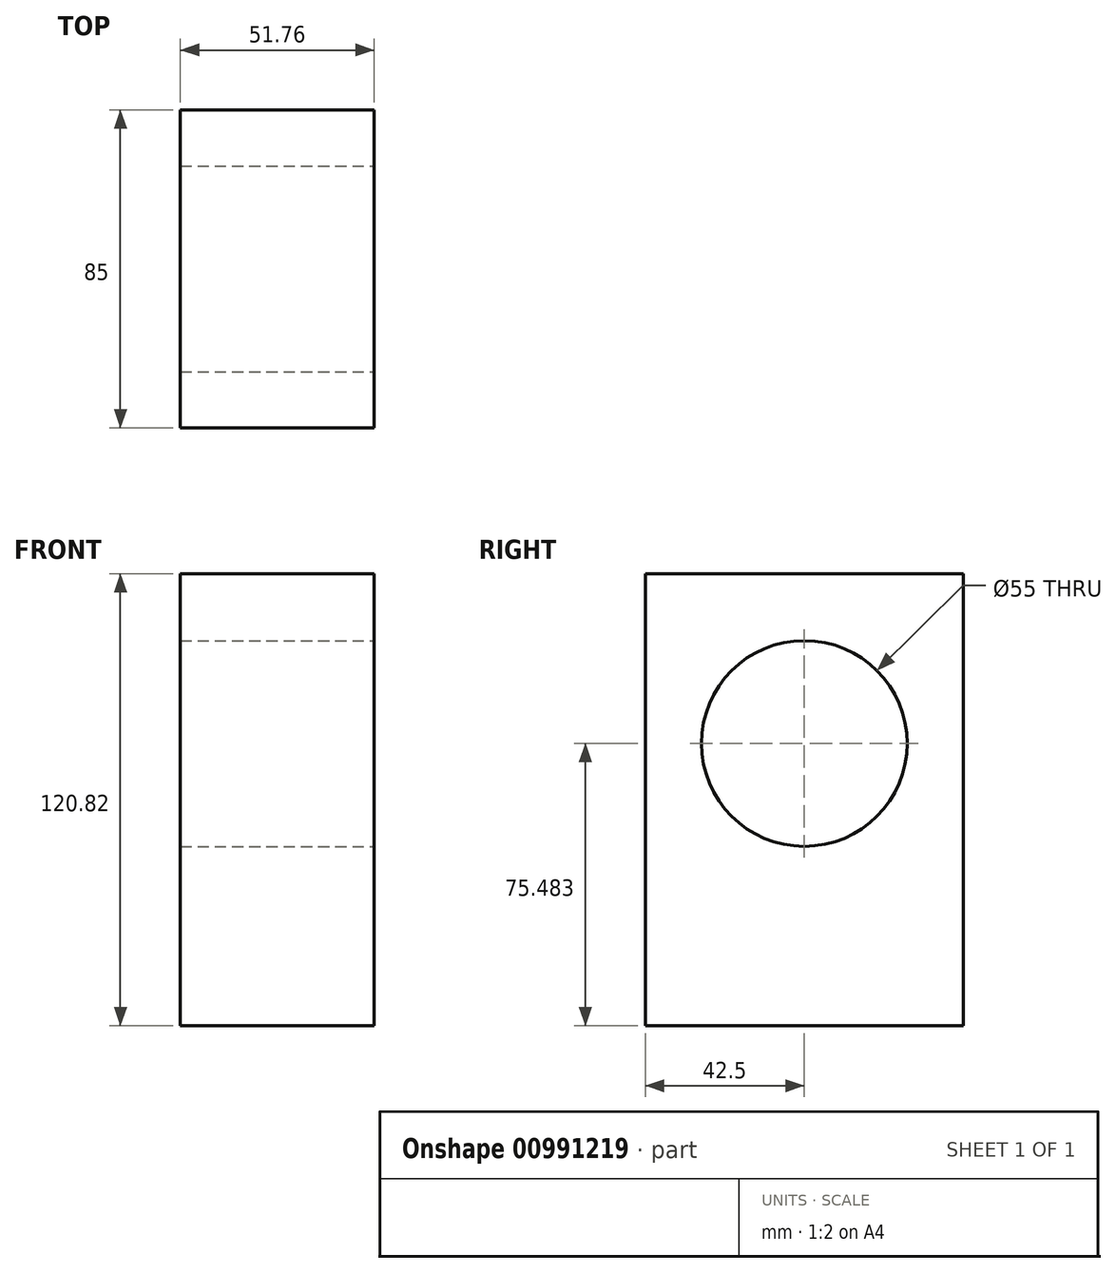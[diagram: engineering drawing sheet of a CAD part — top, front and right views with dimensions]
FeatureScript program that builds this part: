
annotation { "Feature Type Name" : "Feature", "Feature Type Description" : "" }
export const myFeature = defineFeature(function(context is Context, id is Id, definition is map)
    precondition{}
    {
        {
            var Q0;
            Q0=qCreatedBy(makeId("Front.planeOp"),FACE);
            var sketch = newSketch(context, id + "F0", { "sketchPlane" : qUnion([Q0])});
            skLineSegment(sketch, "E0.bottom", {"start": v(0, -39.2) * mm, "end": v(51.76, -39.2) * mm});
            skLineSegment(sketch, "E0.top", {"start": v(0, 81.6) * mm, "end": v(51.76, 81.6) * mm});
            skLineSegment(sketch, "E0.left", {"start": v(0, -39.2) * mm, "end": v(0, 81.6) * mm});
            skLineSegment(sketch, "E0.right", {"start": v(51.76, -39.2) * mm, "end": v(51.76, 81.6) * mm});
            skSolve(sketch);
        }
        {
            var Q0;
            Q0=makeQuery(id+"F0.imprint","IMPRINT",FACE,{"disambiguationData":[TD([[makeQuery(id+"F0.imprint","IMPRINT",EDGE,{"derivedFrom":sQuery(id+"F0.wireOp",EDGE,"E0.bottom")}),1.0]])]});
            var sketch = newSketch(context, id + "F1", { "sketchPlane" : qUnion([Q0])});
            skSolve(sketch);
        }
        {
            var Q0;
            Q0=makeQuery(id+"F1.imprint","IMPRINT",FACE,{"disambiguationData":[TD([[makeQuery(id+"F1.imprint","IMPRINT",EDGE,{"derivedFrom":makeQuery(id+"F0.imprint","IMPRINT",EDGE,{"derivedFrom":sQuery(id+"F0.wireOp",EDGE,"E0.bottom")})}),1.0]])]});
            extrude(context, id + "F2", {"entities" : qUnion([Q0]), "depth" : 85 * mm, "offsetDistance" : 25 * mm});
        }
        {
            var Q0;
            Q0=makeQuery(id+"F2.opExtrude","SWEPT_FACE",FACE,{"disambiguationData":[OSD([sQuery(id+"F0.wireOp",EDGE,"E0.right")])]});
            var sketch = newSketch(context, id + "F3", { "sketchPlane" : qUnion([Q0])});
            skCircle(sketch, "E1", {"center": v(-42.5, 36.27) * mm, "radius": 32.2 * mm});
            skPoint(sketch, "E1.centerSnap0", {"position": v(-42.5, 81.6) * mm});
            skSolve(sketch);
        }
        {
            var Q0;
            Q0=sQuery(id+"F3.wireOp",VERTEX,"E1.center");
            var Q1;
            Q1=makeQuery(id+"F2.opExtrude","SWEPT_BODY",BODY,{"disambiguationData":[OSD([sQuery(id+"F0.wireOp",EDGE,"E0.bottom"),sQuery(id+"F0.wireOp",EDGE,"E0.top"),sQuery(id+"F0.wireOp",EDGE,"E0.left"),sQuery(id+"F0.wireOp",EDGE,"E0.right")])]});
            hole(context, id + "F4", {"style" : HoleStyle.SIMPLE, "endStyle" : HoleEndStyle.THROUGH, "holeDiameter" : 55 * mm, "majorDiameter" : 5 * mm, "isTappedThrough" : true, "tappedDepth" : 12 * mm, "tapClearance" : 3, "locations" : qUnion([Q0]), "scope" : qUnion([Q1])});
        }
    });
